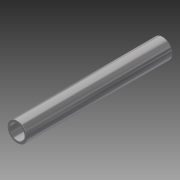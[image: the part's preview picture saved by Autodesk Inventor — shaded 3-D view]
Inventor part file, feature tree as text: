
AUTODESK INVENTOR PART (.ipt)
format: ipt  version: 2016 SP1 (Build 200210100, 210)  size: 107,008 bytes
history: native  units: in
note: dims shown in document units (in); Inventor stores cm internally (conversion verified against a paired STEP export)
features: other x21, revolve x1, sketch x1
ambient origin geometry x8: Origin, YZ Plane, XZ Plane, XY Plane, X Axis, Y Axis, Z Axis, Center Point
bodies: Solid1 (feature_tree)
feature tree (23):
  revolve  "Revolution1"  [1 undecoded]
  other  "cap_XY"
  other  "cap_YZ"
  other  "cap_ZX"
  other  "cap_X"
  other  "cap_Y"
  other  "cap_Z"
  other  "cap_Center"
  other  "ctr_XY"
  other  "ctr_YZ"
  other  "ctr_ZX"
  other  "ctr_X"
  other  "ctr_Y"
  other  "ctr_Z"
  other  "ctr_Center"
  other  "hd_XY"
  other  "hd_YZ"
  other  "hd_ZX"
  other  "hd_X"
  other  "hd_Y"
  other  "hd_Z"
  other  "hd_Center"
  sketch  "Sketch_2"  dims[d0=360.0deg d1=0.0in d2=0.0in]
note: 1 required parameter value undecoded (feature->parameter linkage not recoverable at this tier; creation-order binding heuristic only, values carry confidence <= 0.55)
